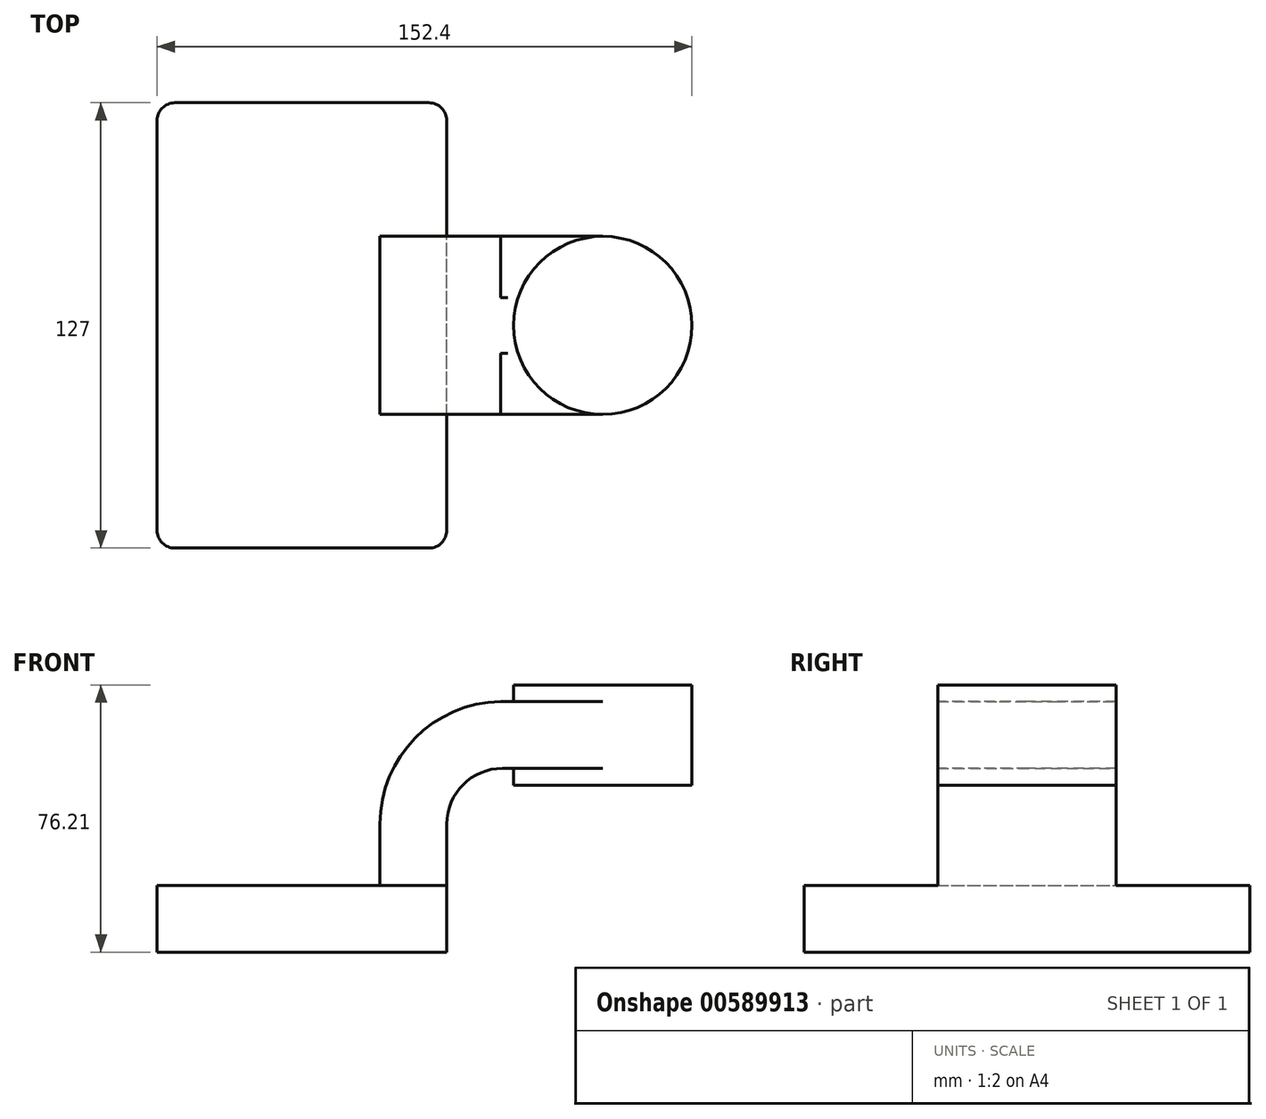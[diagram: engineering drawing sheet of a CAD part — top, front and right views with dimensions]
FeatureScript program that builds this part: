
annotation { "Feature Type Name" : "Feature", "Feature Type Description" : "" }
export const myFeature = defineFeature(function(context is Context, id is Id, definition is map)
    precondition{}
    {
        {
            var Q0;
            Q0=qCreatedBy(makeId("Front.planeOp"),FACE);
            var sketch = newSketch(context, id + "F0", { "sketchPlane" : qUnion([Q0])});
            skLineSegment(sketch, "E0.bottom", {"start": v(-41.28, 9.52) * mm, "end": v(41.27, 9.53) * mm});
            skLineSegment(sketch, "E0.top", {"start": v(-41.28, -9.53) * mm, "end": v(41.28, -9.53) * mm});
            skLineSegment(sketch, "E0.left", {"start": v(-41.28, 9.52) * mm, "end": v(-41.27, -9.53) * mm});
            skLineSegment(sketch, "E0.right", {"start": v(41.28, 9.53) * mm, "end": v(41.28, -9.52) * mm});
            skPoint(sketch, "E0.middle", {"position": v(0, 0) * mm});
            skLineSegment(sketch, "E1", {"start": v(41.27, 9.53) * mm, "end": v(41.27, 27) * mm});
            skLineSegment(sketch, "E2", {"start": v(57.15, 42.88) * mm, "end": v(85.72, 42.88) * mm});
            skLineSegment(sketch, "E3.bottom", {"start": v(111.12, 66.68) * mm, "end": v(60.32, 66.68) * mm});
            skLineSegment(sketch, "E3.top", {"start": v(111.12, 38.1) * mm, "end": v(60.32, 38.1) * mm});
            skLineSegment(sketch, "E3.left", {"start": v(111.12, 66.68) * mm, "end": v(111.12, 38.1) * mm});
            skLineSegment(sketch, "E3.right", {"start": v(60.32, 66.68) * mm, "end": v(60.32, 38.1) * mm});
            skPoint(sketch, "E3.middle", {"position": v(85.72, 52.39) * mm});
            skArc(sketch, "E4", {"start": v(41.27, 27) * mm, "mid": v(45.92, 38.23) * mm, "end": v(57.15, 42.88) * mm});
            skLineSegment(sketch, "E5.0", {"start": v(57.15, 61.93) * mm, "end": v(85.72, 61.93) * mm});
            skArc(sketch, "E5.1", {"start": v(22.22, 27) * mm, "mid": v(32.45, 51.7) * mm, "end": v(57.15, 61.93) * mm});
            skLineSegment(sketch, "E5.2", {"start": v(22.22, 9.53) * mm, "end": v(22.22, 27) * mm});
            skLineSegment(sketch, "E6", {"start": v(85.72, 38.1) * mm, "end": v(85.72, 66.68) * mm});
            skFitSpline(sketch, "E7", {"points": [v(-41.28, 9.52) * mm, v(60.32, 61.93) * mm], "startDerivative": vector(-1.45, 150.62) * mm, "endDerivative": vector(120.97, -0.1) * mm});
            skSolve(sketch);
        }
        {
            var Q0;
            Q0=makeQuery(id+"F0.imprint","IMPRINT",FACE,{"disambiguationData":[TD([[makeQuery(id+"F0.imprint","IMPRINT",EDGE,{"derivedFrom":sQuery(id+"F0.wireOp",EDGE,"E0.top")}),1.0]])]});
            extrude(context, id + "F1", {"entities" : qUnion([Q0]), "endBound" : BoundingType.SYMMETRIC, "depth" : 127 * mm, "offsetDistance" : 25.4 * mm});
        }
        {
            var Q0;
            {var subQ5=sQuery(id+"F0.wireOp",EDGE,"E1");Q0=makeQuery(id+"F0.imprint","IMPRINT",FACE,{"disambiguationData":[TD([[makeQuery(id+"F0.imprint","IMPRINT",EDGE,{"derivedFrom":subQ5}),1.0]])]});}
            var Q1;
            {var subQ0=sQuery(id+"F0.wireOp",EDGE,"E6");var subQ1=sQuery(id+"F0.wireOp",EDGE,"E2");var subQ2=makeQuery(id+"F0.imprint","INTERSECT",VERTEX,{"derivedFrom":[subQ1,subQ0]});Q1=makeQuery(id+"F0.imprint","IMPRINT",FACE,{"disambiguationData":[TD([[makeQuery(id+"F0.imprint","IMPRINT",EDGE,{"disambiguationData":[TD([[subQ2,1.0]])],"derivedFrom":subQ1}),1.0]])]});}
            extrude(context, id + "F2", {"entities" : qUnion([Q0, Q1]), "operationType" : NewBodyOperationType.ADD, "endBound" : BoundingType.SYMMETRIC, "depth" : 50.8 * mm, "offsetDistance" : 25.4 * mm});
        }
        {
            var Q0;
            {var subQ0=sQuery(id+"F0.wireOp",EDGE,"E5.1");Q0=makeQuery(id+"F0.imprint","IMPRINT",FACE,{"disambiguationData":[TD([[makeQuery(id+"F0.imprint","IMPRINT",EDGE,{"derivedFrom":subQ0}),1.0]])]});}
            extrude(context, id + "F3", {"entities" : qUnion([Q0]), "operationType" : NewBodyOperationType.ADD, "endBound" : BoundingType.SYMMETRIC, "depth" : 15.88 * mm, "offsetDistance" : 25.4 * mm});
        }
        {
            var Q0;
            {var subQ4=sQuery(id+"F0.wireOp",EDGE,"E3.left");Q0=makeQuery(id+"F0.imprint","IMPRINT",FACE,{"disambiguationData":[TD([[makeQuery(id+"F0.imprint","IMPRINT",EDGE,{"derivedFrom":subQ4}),-1.0]])]});}
            var Q1;
            Q1=sQuery(id+"F0.wireOp",EDGE,"E6");
            revolve(context, id + "F4", {"operationType" : NewBodyOperationType.ADD, "entities" : qUnion([Q0]), "axis" : qUnion([Q1]), "revolveType" : RevolveType.FULL});
        }
        {
            var Q0;
            Q0=makeQuery(id+"F1.opExtrude","CAP_EDGE",EDGE,{"disambiguationData":[OSD([sQuery(id+"F0.wireOp",EDGE,"E0.right")])],"isStart":false});
            var Q1;
            Q1=makeQuery(id+"F1.opExtrude","CAP_EDGE",EDGE,{"disambiguationData":[OSD([sQuery(id+"F0.wireOp",EDGE,"E0.left")])],"isStart":false});
            var Q2;
            Q2=makeQuery(id+"F1.opExtrude","CAP_EDGE",EDGE,{"disambiguationData":[OSD([sQuery(id+"F0.wireOp",EDGE,"E0.right")])],"isStart":true});
            var Q3;
            Q3=makeQuery(id+"F1.opExtrude","CAP_EDGE",EDGE,{"disambiguationData":[OSD([sQuery(id+"F0.wireOp",EDGE,"E0.left")])],"isStart":true});
            fillet(context, id + "F5", {"entities" : qUnion([Q0, Q1, Q2, Q3]), "radius" : 5.08 * mm, "tangentPropagation" : true, "allowEdgeOverflow" : false});
        }
    });
